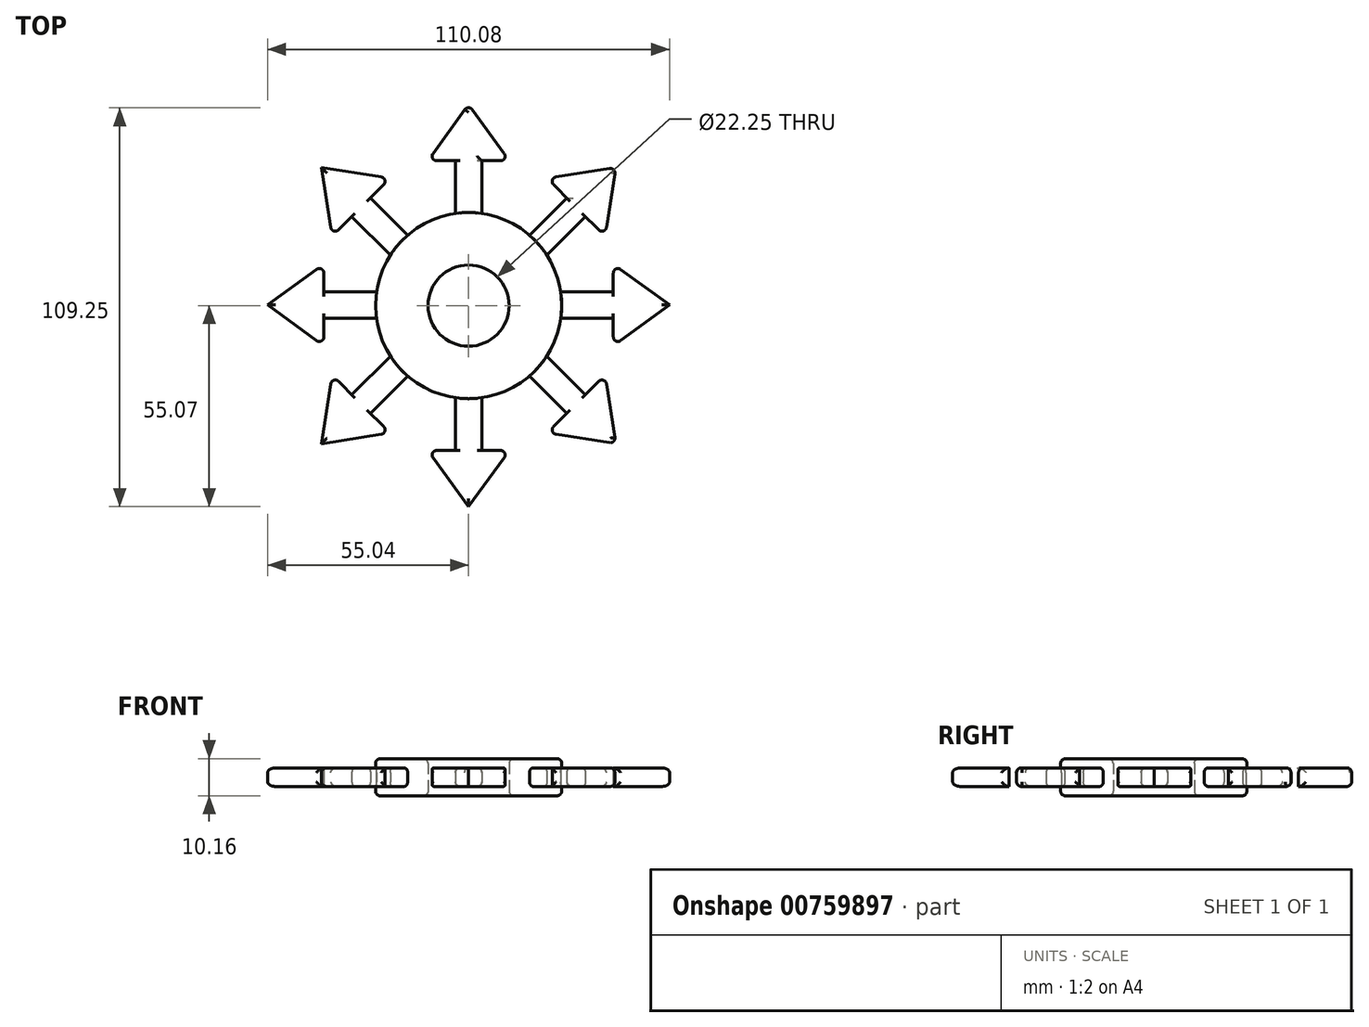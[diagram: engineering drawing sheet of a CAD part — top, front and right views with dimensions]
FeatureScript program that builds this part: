
annotation { "Feature Type Name" : "Feature", "Feature Type Description" : "" }
export const myFeature = defineFeature(function(context is Context, id is Id, definition is map)
    precondition{}
    {
        {
            var Q0;
            Q0=qCreatedBy(makeId("Top.planeOp"),FACE);
            var sketch = newSketch(context, id + "F0", { "sketchPlane" : qUnion([Q0])});
            skPoint(sketch, "E0.middle", {"position": v(0, 0) * mm});
            skCircle(sketch, "E1", {"center": v(0, 0) * mm, "radius": 25.5 * mm});
            skLineSegment(sketch, "E2", {"start": v(3.6, 25.24) * mm, "end": v(3.6, 39.67) * mm});
            skLineSegment(sketch, "E3", {"start": v(-3.6, 25.24) * mm, "end": v(-3.6, 39.67) * mm});
            skLineSegment(sketch, "E4", {"start": v(-3.6, 39.67) * mm, "end": v(-11.23, 39.67) * mm});
            skLineSegment(sketch, "E5", {"start": v(-11.23, 39.67) * mm, "end": v(0, 55.07) * mm});
            skLineSegment(sketch, "E6.MirrorCS", {"start": v(11.23, 39.67) * mm, "end": v(0, 55.07) * mm});
            skLineSegment(sketch, "E7.MirrorCS", {"start": v(3.6, 39.67) * mm, "end": v(11.23, 39.67) * mm});
            skLineSegment(sketch, "E8.MirrorCS", {"start": v(3.6, -25.24) * mm, "end": v(3.6, -39.67) * mm});
            skLineSegment(sketch, "E9.MirrorCS", {"start": v(-3.6, -25.24) * mm, "end": v(-3.6, -39.67) * mm});
            skLineSegment(sketch, "E10.MirrorCS", {"start": v(-11.23, -39.67) * mm, "end": v(0, -55.07) * mm});
            skLineSegment(sketch, "E11.MirrorCS", {"start": v(11.23, -39.67) * mm, "end": v(0, -55.07) * mm});
            skLineSegment(sketch, "E12.MirrorCS", {"start": v(3.6, -39.67) * mm, "end": v(11.23, -39.67) * mm});
            skLineSegment(sketch, "E13.MirrorCS", {"start": v(-3.6, -39.67) * mm, "end": v(-11.23, -39.67) * mm});
            skLineSegment(sketch, "E14", {"start": v(25.22, -3.44) * mm, "end": v(39.64, -3.44) * mm});
            skLineSegment(sketch, "E15", {"start": v(25.22, 3.77) * mm, "end": v(39.64, 3.77) * mm});
            skLineSegment(sketch, "E16", {"start": v(39.64, 3.77) * mm, "end": v(39.64, 11.4) * mm});
            skLineSegment(sketch, "E17", {"start": v(39.64, 11.4) * mm, "end": v(55.04, 0.17) * mm});
            skLineSegment(sketch, "E18.MirrorCS", {"start": v(39.64, -11.06) * mm, "end": v(55.04, 0.17) * mm});
            skLineSegment(sketch, "E19.MirrorCS", {"start": v(39.64, -3.44) * mm, "end": v(39.64, -11.06) * mm});
            skLineSegment(sketch, "E20.MirrorCS", {"start": v(-39.64, 11.4) * mm, "end": v(-55.04, 0.17) * mm});
            skLineSegment(sketch, "E21.MirrorCS", {"start": v(-39.64, -11.06) * mm, "end": v(-55.04, 0.17) * mm});
            skLineSegment(sketch, "E22.MirrorCS", {"start": v(-39.64, -3.44) * mm, "end": v(-39.64, -11.06) * mm});
            skLineSegment(sketch, "E23.MirrorCS", {"start": v(-39.64, 3.77) * mm, "end": v(-39.64, 11.4) * mm});
            skLineSegment(sketch, "E24.MirrorCS", {"start": v(-25.22, 3.77) * mm, "end": v(-39.64, 3.77) * mm});
            skLineSegment(sketch, "E25.MirrorCS", {"start": v(-25.22, -3.44) * mm, "end": v(-39.64, -3.44) * mm});
            skLineSegment(sketch, "E26", {"start": v(16.7, 19.28) * mm, "end": v(26.9, 29.48) * mm});
            skLineSegment(sketch, "E27", {"start": v(26.9, 29.48) * mm, "end": v(21.5, 34.86) * mm});
            skLineSegment(sketch, "E28", {"start": v(21.5, 34.86) * mm, "end": v(40.33, 37.82) * mm});
            skLineSegment(sketch, "E29.MirrorCS", {"start": v(37.38, 18.99) * mm, "end": v(40.33, 37.82) * mm});
            skLineSegment(sketch, "E30.MirrorCS", {"start": v(32, 24.38) * mm, "end": v(37.38, 18.99) * mm});
            skLineSegment(sketch, "E31.MirrorCS", {"start": v(-16.7, 19.28) * mm, "end": v(-26.9, 29.48) * mm});
            skLineSegment(sketch, "E32.MirrorCS", {"start": v(-37.38, 18.99) * mm, "end": v(-40.33, 37.82) * mm});
            skLineSegment(sketch, "E33.MirrorCS", {"start": v(-21.5, 34.86) * mm, "end": v(-40.33, 37.82) * mm});
            skLineSegment(sketch, "E34.MirrorCS", {"start": v(-26.9, 29.48) * mm, "end": v(-21.5, 34.86) * mm});
            skLineSegment(sketch, "E35.MirrorCS", {"start": v(-32, 24.38) * mm, "end": v(-37.38, 18.99) * mm});
            skLineSegment(sketch, "E36", {"start": v(-32, 24.38) * mm, "end": v(-21.43, 13.82) * mm});
            skLineSegment(sketch, "E37", {"start": v(32, 24.38) * mm, "end": v(21.43, 13.82) * mm});
            skLineSegment(sketch, "E38.MirrorCS", {"start": v(-16.7, -19.28) * mm, "end": v(-26.9, -29.48) * mm});
            skLineSegment(sketch, "E39.MirrorCS", {"start": v(-32, -24.38) * mm, "end": v(-21.43, -13.82) * mm});
            skLineSegment(sketch, "E40.MirrorCS", {"start": v(-37.38, -18.99) * mm, "end": v(-40.33, -37.82) * mm});
            skLineSegment(sketch, "E41.MirrorCS", {"start": v(-21.5, -34.86) * mm, "end": v(-40.33, -37.82) * mm});
            skLineSegment(sketch, "E42.MirrorCS", {"start": v(-26.9, -29.48) * mm, "end": v(-21.5, -34.86) * mm});
            skLineSegment(sketch, "E43.MirrorCS", {"start": v(-32, -24.38) * mm, "end": v(-37.38, -18.99) * mm});
            skLineSegment(sketch, "E44.MirrorCS", {"start": v(37.38, -18.99) * mm, "end": v(40.33, -37.82) * mm});
            skLineSegment(sketch, "E45.MirrorCS", {"start": v(21.5, -34.86) * mm, "end": v(40.33, -37.82) * mm});
            skLineSegment(sketch, "E46.MirrorCS", {"start": v(16.7, -19.28) * mm, "end": v(26.9, -29.48) * mm});
            skLineSegment(sketch, "E47.MirrorCS", {"start": v(32, -24.38) * mm, "end": v(21.43, -13.82) * mm});
            skLineSegment(sketch, "E48.MirrorCS", {"start": v(26.9, -29.48) * mm, "end": v(21.5, -34.86) * mm});
            skLineSegment(sketch, "E49.MirrorCS", {"start": v(32, -24.38) * mm, "end": v(37.38, -18.99) * mm});
            skCircle(sketch, "E50", {"center": v(0, 0) * mm, "radius": 11.13 * mm});
            skSolve(sketch);
        }
        {
            var Q0;
            Q0=makeQuery(id+"F0.imprint","IMPRINT",FACE,{"disambiguationData":[TD([[makeQuery(id+"F0.imprint","IMPRINT",EDGE,{"derivedFrom":sQuery(id+"F0.wireOp",EDGE,"E50")}),-1.0]])]});
            extrude(context, id + "F1", {"entities" : qUnion([Q0]), "endBound" : BoundingType.SYMMETRIC, "depth" : 10.16 * mm, "offsetDistance" : 25.4 * mm});
        }
        {
            var Q0;
            {var subQ0=sQuery(id+"F0.wireOp",EDGE,"E31.MirrorCS");Q0=makeQuery(id+"F0.imprint","IMPRINT",FACE,{"disambiguationData":[TD([[makeQuery(id+"F0.imprint","IMPRINT",EDGE,{"derivedFrom":subQ0}),1.0]])]});}
            var Q1;
            {var subQ1=sQuery(id+"F0.wireOp",EDGE,"E2");Q1=makeQuery(id+"F0.imprint","IMPRINT",FACE,{"disambiguationData":[TD([[makeQuery(id+"F0.imprint","IMPRINT",EDGE,{"derivedFrom":subQ1}),1.0]])]});}
            var Q2;
            {var subQ0=sQuery(id+"F0.wireOp",EDGE,"E26");Q2=makeQuery(id+"F0.imprint","IMPRINT",FACE,{"disambiguationData":[TD([[makeQuery(id+"F0.imprint","IMPRINT",EDGE,{"derivedFrom":subQ0}),-1.0]])]});}
            var Q3;
            {var subQ0=sQuery(id+"F0.wireOp",EDGE,"E15");Q3=makeQuery(id+"F0.imprint","IMPRINT",FACE,{"disambiguationData":[TD([[makeQuery(id+"F0.imprint","IMPRINT",EDGE,{"derivedFrom":subQ0}),-1.0]])]});}
            var Q4;
            Q4=makeQuery(id+"F0.imprint","IMPRINT",FACE,{"disambiguationData":[TD([[makeQuery(id+"F0.imprint","IMPRINT",EDGE,{"derivedFrom":sQuery(id+"F0.wireOp",EDGE,"E44.MirrorCS")}),-1.0]])]});
            var Q5;
            {var subQ1=sQuery(id+"F0.wireOp",EDGE,"E8.MirrorCS");Q5=makeQuery(id+"F0.imprint","IMPRINT",FACE,{"disambiguationData":[TD([[makeQuery(id+"F0.imprint","IMPRINT",EDGE,{"derivedFrom":subQ1}),-1.0]])]});}
            var Q6;
            {var subQ1=sQuery(id+"F0.wireOp",EDGE,"E38.MirrorCS");Q6=makeQuery(id+"F0.imprint","IMPRINT",FACE,{"disambiguationData":[TD([[makeQuery(id+"F0.imprint","IMPRINT",EDGE,{"derivedFrom":subQ1}),-1.0]])]});}
            var Q7;
            Q7=makeQuery(id+"F0.imprint","IMPRINT",FACE,{"disambiguationData":[TD([[makeQuery(id+"F0.imprint","IMPRINT",EDGE,{"derivedFrom":sQuery(id+"F0.wireOp",EDGE,"E20.MirrorCS")}),1.0]])]});
            extrude(context, id + "F2", {"entities" : qUnion([Q0, Q1, Q2, Q3, Q4, Q5, Q6, Q7]), "operationType" : NewBodyOperationType.ADD, "endBound" : BoundingType.SYMMETRIC, "depth" : 5.08 * mm, "offsetDistance" : 25.4 * mm});
        }
        {
            var Q0;
            Q0=makeQuery(id+"F1.opExtrude","CAP_FACE",FACE,{"disambiguationData":[OSD([sQuery(id+"F0.wireOp",EDGE,"E1"),sQuery(id+"F0.wireOp",EDGE,"E50")])],"isStart":false});
            var Q1;
            Q1=makeQuery(id+"F1.opExtrude","CAP_EDGE",EDGE,{"disambiguationData":[OSD([sQuery(id+"F0.wireOp",EDGE,"E1")])],"isStart":true});
            var Q2;
            Q2=makeQuery(id+"F2.opExtrude","CAP_EDGE",EDGE,{"disambiguationData":[OSD([sQuery(id+"F0.wireOp",EDGE,"E25.MirrorCS")])],"isStart":false});
            var Q3;
            Q3=makeQuery(id+"F2.opExtrude","CAP_EDGE",EDGE,{"disambiguationData":[OSD([sQuery(id+"F0.wireOp",EDGE,"E25.MirrorCS")])],"isStart":true});
            var Q4;
            Q4=makeQuery(id+"F2.opExtrude","CAP_EDGE",EDGE,{"disambiguationData":[OSD([sQuery(id+"F0.wireOp",EDGE,"E24.MirrorCS")])],"isStart":true});
            var Q5;
            Q5=makeQuery(id+"F2.opExtrude","CAP_EDGE",EDGE,{"disambiguationData":[OSD([sQuery(id+"F0.wireOp",EDGE,"E24.MirrorCS")])],"isStart":false});
            var Q6;
            Q6=makeQuery(id+"F2.opExtrude","CAP_EDGE",EDGE,{"disambiguationData":[OSD([sQuery(id+"F0.wireOp",EDGE,"E38.MirrorCS")])],"isStart":false});
            var Q7;
            Q7=makeQuery(id+"F2.opExtrude","CAP_EDGE",EDGE,{"disambiguationData":[OSD([sQuery(id+"F0.wireOp",EDGE,"E39.MirrorCS")])],"isStart":false});
            var Q8;
            Q8=makeQuery(id+"F2.opExtrude","CAP_EDGE",EDGE,{"disambiguationData":[OSD([sQuery(id+"F0.wireOp",EDGE,"E38.MirrorCS")])],"isStart":true});
            var Q9;
            Q9=makeQuery(id+"F2.opExtrude","CAP_EDGE",EDGE,{"disambiguationData":[OSD([sQuery(id+"F0.wireOp",EDGE,"E39.MirrorCS")])],"isStart":true});
            var Q10;
            Q10=makeQuery(id+"F2.opExtrude","CAP_EDGE",EDGE,{"disambiguationData":[OSD([sQuery(id+"F0.wireOp",EDGE,"E9.MirrorCS")])],"isStart":true});
            var Q11;
            Q11=makeQuery(id+"F2.opExtrude","CAP_EDGE",EDGE,{"disambiguationData":[OSD([sQuery(id+"F0.wireOp",EDGE,"E8.MirrorCS")])],"isStart":true});
            var Q12;
            Q12=makeQuery(id+"F2.opExtrude","CAP_EDGE",EDGE,{"disambiguationData":[OSD([sQuery(id+"F0.wireOp",EDGE,"E9.MirrorCS")])],"isStart":false});
            var Q13;
            Q13=makeQuery(id+"F2.opExtrude","CAP_EDGE",EDGE,{"disambiguationData":[OSD([sQuery(id+"F0.wireOp",EDGE,"E8.MirrorCS")])],"isStart":false});
            var Q14;
            Q14=makeQuery(id+"F2.opExtrude","CAP_EDGE",EDGE,{"disambiguationData":[OSD([sQuery(id+"F0.wireOp",EDGE,"E46.MirrorCS")])],"isStart":true});
            var Q15;
            Q15=makeQuery(id+"F2.opExtrude","CAP_EDGE",EDGE,{"disambiguationData":[OSD([sQuery(id+"F0.wireOp",EDGE,"E46.MirrorCS")])],"isStart":false});
            var Q16;
            Q16=makeQuery(id+"F2.opExtrude","CAP_EDGE",EDGE,{"disambiguationData":[OSD([sQuery(id+"F0.wireOp",EDGE,"E47.MirrorCS")])],"isStart":false});
            var Q17;
            Q17=makeQuery(id+"F2.opExtrude","CAP_EDGE",EDGE,{"disambiguationData":[OSD([sQuery(id+"F0.wireOp",EDGE,"E47.MirrorCS")])],"isStart":true});
            var Q18;
            Q18=makeQuery(id+"F2.opExtrude","CAP_EDGE",EDGE,{"disambiguationData":[OSD([sQuery(id+"F0.wireOp",EDGE,"E14")])],"isStart":true});
            var Q19;
            Q19=makeQuery(id+"F2.opExtrude","CAP_EDGE",EDGE,{"disambiguationData":[OSD([sQuery(id+"F0.wireOp",EDGE,"E14")])],"isStart":false});
            var Q20;
            Q20=makeQuery(id+"F2.opExtrude","CAP_EDGE",EDGE,{"disambiguationData":[OSD([sQuery(id+"F0.wireOp",EDGE,"E15")])],"isStart":true});
            var Q21;
            Q21=makeQuery(id+"F2.opExtrude","CAP_EDGE",EDGE,{"disambiguationData":[OSD([sQuery(id+"F0.wireOp",EDGE,"E15")])],"isStart":false});
            var Q22;
            Q22=makeQuery(id+"F2.opExtrude","CAP_EDGE",EDGE,{"disambiguationData":[OSD([sQuery(id+"F0.wireOp",EDGE,"E37")])],"isStart":true});
            var Q23;
            Q23=makeQuery(id+"F2.opExtrude","CAP_EDGE",EDGE,{"disambiguationData":[OSD([sQuery(id+"F0.wireOp",EDGE,"E37")])],"isStart":false});
            var Q24;
            Q24=makeQuery(id+"F2.opExtrude","CAP_EDGE",EDGE,{"disambiguationData":[OSD([sQuery(id+"F0.wireOp",EDGE,"E26")])],"isStart":true});
            var Q25;
            Q25=makeQuery(id+"F2.opExtrude","CAP_EDGE",EDGE,{"disambiguationData":[OSD([sQuery(id+"F0.wireOp",EDGE,"E26")])],"isStart":false});
            var Q26;
            Q26=makeQuery(id+"F2.opExtrude","CAP_EDGE",EDGE,{"disambiguationData":[OSD([sQuery(id+"F0.wireOp",EDGE,"E2")])],"isStart":true});
            var Q27;
            Q27=makeQuery(id+"F2.opExtrude","CAP_EDGE",EDGE,{"disambiguationData":[OSD([sQuery(id+"F0.wireOp",EDGE,"E2")])],"isStart":false});
            var Q28;
            Q28=makeQuery(id+"F2.opExtrude","CAP_EDGE",EDGE,{"disambiguationData":[OSD([sQuery(id+"F0.wireOp",EDGE,"E3")])],"isStart":false});
            var Q29;
            Q29=makeQuery(id+"F2.opExtrude","CAP_EDGE",EDGE,{"disambiguationData":[OSD([sQuery(id+"F0.wireOp",EDGE,"E3")])],"isStart":true});
            var Q30;
            Q30=makeQuery(id+"F2.opExtrude","CAP_EDGE",EDGE,{"disambiguationData":[OSD([sQuery(id+"F0.wireOp",EDGE,"E31.MirrorCS")])],"isStart":true});
            var Q31;
            Q31=makeQuery(id+"F2.opExtrude","CAP_EDGE",EDGE,{"disambiguationData":[OSD([sQuery(id+"F0.wireOp",EDGE,"E31.MirrorCS")])],"isStart":false});
            var Q32;
            Q32=makeQuery(id+"F2.opExtrude","CAP_EDGE",EDGE,{"disambiguationData":[OSD([sQuery(id+"F0.wireOp",EDGE,"E36")])],"isStart":true});
            var Q33;
            Q33=makeQuery(id+"F2.opExtrude","CAP_EDGE",EDGE,{"disambiguationData":[OSD([sQuery(id+"F0.wireOp",EDGE,"E36")])],"isStart":false});
            var Q34;
            Q34=makeQuery(id+"F2.opExtrude","CAP_EDGE",EDGE,{"disambiguationData":[OSD([sQuery(id+"F0.wireOp",EDGE,"E32.MirrorCS")])],"isStart":false});
            var Q35;
            Q35=makeQuery(id+"F2.opExtrude","CAP_EDGE",EDGE,{"disambiguationData":[OSD([sQuery(id+"F0.wireOp",EDGE,"E32.MirrorCS")])],"isStart":true});
            var Q36;
            Q36=makeQuery(id+"F2.opExtrude","CAP_EDGE",EDGE,{"disambiguationData":[OSD([sQuery(id+"F0.wireOp",EDGE,"E33.MirrorCS")])],"isStart":true});
            var Q37;
            Q37=makeQuery(id+"F2.opExtrude","CAP_EDGE",EDGE,{"disambiguationData":[OSD([sQuery(id+"F0.wireOp",EDGE,"E33.MirrorCS")])],"isStart":false});
            var Q38;
            Q38=makeQuery(id+"F2.opExtrude","SWEPT_EDGE",EDGE,{"disambiguationData":[OSD([sQuery(id+"F0.wireOp",EDGE,"E32.MirrorCS"),sQuery(id+"F0.wireOp",EDGE,"E35.MirrorCS")])]});
            var Q39;
            Q39=makeQuery(id+"F2.opExtrude","SWEPT_EDGE",EDGE,{"disambiguationData":[OSD([sQuery(id+"F0.wireOp",EDGE,"E33.MirrorCS"),sQuery(id+"F0.wireOp",EDGE,"E34.MirrorCS")])]});
            var Q40;
            Q40=makeQuery(id+"F2.opExtrude","SWEPT_EDGE",EDGE,{"disambiguationData":[OSD([sQuery(id+"F0.wireOp",EDGE,"E4"),sQuery(id+"F0.wireOp",EDGE,"E5")])]});
            var Q41;
            Q41=makeQuery(id+"F2.opExtrude","SWEPT_EDGE",EDGE,{"disambiguationData":[OSD([sQuery(id+"F0.wireOp",EDGE,"E6.MirrorCS"),sQuery(id+"F0.wireOp",EDGE,"E7.MirrorCS")])]});
            var Q42;
            Q42=makeQuery(id+"F2.opExtrude","CAP_EDGE",EDGE,{"disambiguationData":[OSD([sQuery(id+"F0.wireOp",EDGE,"E6.MirrorCS")])],"isStart":true});
            var Q43;
            Q43=makeQuery(id+"F2.opExtrude","CAP_EDGE",EDGE,{"disambiguationData":[OSD([sQuery(id+"F0.wireOp",EDGE,"E5")])],"isStart":false});
            var Q44;
            Q44=makeQuery(id+"F2.opExtrude","CAP_EDGE",EDGE,{"disambiguationData":[OSD([sQuery(id+"F0.wireOp",EDGE,"E5")])],"isStart":true});
            var Q45;
            Q45=makeQuery(id+"F2.opExtrude","CAP_EDGE",EDGE,{"disambiguationData":[OSD([sQuery(id+"F0.wireOp",EDGE,"E29.MirrorCS")])],"isStart":true});
            var Q46;
            Q46=makeQuery(id+"F2.opExtrude","CAP_EDGE",EDGE,{"disambiguationData":[OSD([sQuery(id+"F0.wireOp",EDGE,"E29.MirrorCS")])],"isStart":false});
            var Q47;
            Q47=makeQuery(id+"F2.opExtrude","CAP_EDGE",EDGE,{"disambiguationData":[OSD([sQuery(id+"F0.wireOp",EDGE,"E28")])],"isStart":false});
            var Q48;
            Q48=makeQuery(id+"F2.opExtrude","SWEPT_EDGE",EDGE,{"disambiguationData":[OSD([sQuery(id+"F0.wireOp",EDGE,"E27"),sQuery(id+"F0.wireOp",EDGE,"E28")])]});
            var Q49;
            Q49=makeQuery(id+"F2.opExtrude","SWEPT_EDGE",EDGE,{"disambiguationData":[OSD([sQuery(id+"F0.wireOp",EDGE,"E29.MirrorCS"),sQuery(id+"F0.wireOp",EDGE,"E30.MirrorCS")])]});
            var Q50;
            Q50=makeQuery(id+"F2.opExtrude","SWEPT_EDGE",EDGE,{"disambiguationData":[OSD([sQuery(id+"F0.wireOp",EDGE,"E16"),sQuery(id+"F0.wireOp",EDGE,"E17")])]});
            var Q51;
            Q51=makeQuery(id+"F2.opExtrude","SWEPT_EDGE",EDGE,{"disambiguationData":[OSD([sQuery(id+"F0.wireOp",EDGE,"E18.MirrorCS"),sQuery(id+"F0.wireOp",EDGE,"E19.MirrorCS")])]});
            var Q52;
            Q52=makeQuery(id+"F2.opExtrude","CAP_EDGE",EDGE,{"disambiguationData":[OSD([sQuery(id+"F0.wireOp",EDGE,"E18.MirrorCS")])],"isStart":false});
            var Q53;
            Q53=makeQuery(id+"F2.opExtrude","CAP_EDGE",EDGE,{"disambiguationData":[OSD([sQuery(id+"F0.wireOp",EDGE,"E17")])],"isStart":false});
            var Q54;
            Q54=makeQuery(id+"F2.opExtrude","CAP_EDGE",EDGE,{"disambiguationData":[OSD([sQuery(id+"F0.wireOp",EDGE,"E18.MirrorCS")])],"isStart":true});
            var Q55;
            Q55=makeQuery(id+"F2.opExtrude","CAP_EDGE",EDGE,{"disambiguationData":[OSD([sQuery(id+"F0.wireOp",EDGE,"E17")])],"isStart":true});
            var Q56;
            Q56=makeQuery(id+"F2.opExtrude","CAP_EDGE",EDGE,{"disambiguationData":[OSD([sQuery(id+"F0.wireOp",EDGE,"E44.MirrorCS")])],"isStart":false});
            var Q57;
            Q57=makeQuery(id+"F2.opExtrude","CAP_EDGE",EDGE,{"disambiguationData":[OSD([sQuery(id+"F0.wireOp",EDGE,"E44.MirrorCS")])],"isStart":true});
            var Q58;
            Q58=makeQuery(id+"F2.opExtrude","SWEPT_EDGE",EDGE,{"disambiguationData":[OSD([sQuery(id+"F0.wireOp",EDGE,"E44.MirrorCS"),sQuery(id+"F0.wireOp",EDGE,"E49.MirrorCS")])]});
            fillet(context, id + "F3", {"entities" : qUnion([Q0, Q1, Q2, Q3, Q4, Q5, Q6, Q7, Q8, Q9, Q10, Q11, Q12, Q13, Q14, Q15, Q16, Q17, Q18, Q19, Q20, Q21, Q22, Q23, Q24, Q25, Q26, Q27, Q28, Q29, Q30, Q31, Q32, Q33, Q34, Q35, Q36, Q37, Q38, Q39, Q40, Q41, Q42, Q43, Q44, Q45, Q46, Q47, Q48, Q49, Q50, Q51, Q52, Q53, Q54, Q55, Q56, Q57, Q58]), "radius" : 1.27 * mm, "tangentPropagation" : true, "allowEdgeOverflow" : false});
        }
        {
            var Q0;
            Q0=makeQuery(id+"F2.opExtrude","CAP_EDGE",EDGE,{"disambiguationData":[OSD([sQuery(id+"F0.wireOp",EDGE,"E45.MirrorCS")])],"isStart":true});
            var Q1;
            Q1=makeQuery(id+"F2.opExtrude","CAP_EDGE",EDGE,{"disambiguationData":[OSD([sQuery(id+"F0.wireOp",EDGE,"E45.MirrorCS")])],"isStart":false});
            var Q2;
            Q2=makeQuery(id+"F2.opExtrude","SWEPT_EDGE",EDGE,{"disambiguationData":[OSD([sQuery(id+"F0.wireOp",EDGE,"E45.MirrorCS"),sQuery(id+"F0.wireOp",EDGE,"E48.MirrorCS")])]});
            var Q3;
            Q3=makeQuery(id+"F2.opExtrude","SWEPT_EDGE",EDGE,{"disambiguationData":[OSD([sQuery(id+"F0.wireOp",EDGE,"E11.MirrorCS"),sQuery(id+"F0.wireOp",EDGE,"E12.MirrorCS")])]});
            var Q4;
            Q4=makeQuery(id+"F2.opExtrude","CAP_EDGE",EDGE,{"disambiguationData":[OSD([sQuery(id+"F0.wireOp",EDGE,"E11.MirrorCS")])],"isStart":false});
            var Q5;
            Q5=makeQuery(id+"F2.opExtrude","CAP_EDGE",EDGE,{"disambiguationData":[OSD([sQuery(id+"F0.wireOp",EDGE,"E11.MirrorCS")])],"isStart":true});
            var Q6;
            Q6=makeQuery(id+"F2.opExtrude","SWEPT_EDGE",EDGE,{"disambiguationData":[OSD([sQuery(id+"F0.wireOp",EDGE,"E10.MirrorCS"),sQuery(id+"F0.wireOp",EDGE,"E13.MirrorCS")])]});
            var Q7;
            Q7=makeQuery(id+"F2.opExtrude","CAP_EDGE",EDGE,{"disambiguationData":[OSD([sQuery(id+"F0.wireOp",EDGE,"E10.MirrorCS")])],"isStart":true});
            var Q8;
            Q8=makeQuery(id+"F2.opExtrude","CAP_EDGE",EDGE,{"disambiguationData":[OSD([sQuery(id+"F0.wireOp",EDGE,"E10.MirrorCS")])],"isStart":false});
            var Q9;
            Q9=makeQuery(id+"F2.opExtrude","SWEPT_EDGE",EDGE,{"disambiguationData":[OSD([sQuery(id+"F0.wireOp",EDGE,"E41.MirrorCS"),sQuery(id+"F0.wireOp",EDGE,"E42.MirrorCS")])]});
            var Q10;
            Q10=makeQuery(id+"F2.opExtrude","CAP_EDGE",EDGE,{"disambiguationData":[OSD([sQuery(id+"F0.wireOp",EDGE,"E41.MirrorCS")])],"isStart":true});
            var Q11;
            Q11=makeQuery(id+"F2.opExtrude","CAP_EDGE",EDGE,{"disambiguationData":[OSD([sQuery(id+"F0.wireOp",EDGE,"E41.MirrorCS")])],"isStart":false});
            var Q12;
            Q12=makeQuery(id+"F2.opExtrude","SWEPT_EDGE",EDGE,{"disambiguationData":[OSD([sQuery(id+"F0.wireOp",EDGE,"E40.MirrorCS"),sQuery(id+"F0.wireOp",EDGE,"E43.MirrorCS")])]});
            var Q13;
            Q13=makeQuery(id+"F2.opExtrude","CAP_EDGE",EDGE,{"disambiguationData":[OSD([sQuery(id+"F0.wireOp",EDGE,"E40.MirrorCS")])],"isStart":true});
            var Q14;
            Q14=makeQuery(id+"F2.opExtrude","CAP_EDGE",EDGE,{"disambiguationData":[OSD([sQuery(id+"F0.wireOp",EDGE,"E40.MirrorCS")])],"isStart":false});
            var Q15;
            Q15=makeQuery(id+"F2.opExtrude","SWEPT_EDGE",EDGE,{"disambiguationData":[OSD([sQuery(id+"F0.wireOp",EDGE,"E20.MirrorCS"),sQuery(id+"F0.wireOp",EDGE,"E23.MirrorCS")])]});
            var Q16;
            Q16=makeQuery(id+"F2.opExtrude","CAP_EDGE",EDGE,{"disambiguationData":[OSD([sQuery(id+"F0.wireOp",EDGE,"E20.MirrorCS")])],"isStart":true});
            var Q17;
            Q17=makeQuery(id+"F2.opExtrude","CAP_EDGE",EDGE,{"disambiguationData":[OSD([sQuery(id+"F0.wireOp",EDGE,"E21.MirrorCS")])],"isStart":false});
            var Q18;
            Q18=makeQuery(id+"F2.opExtrude","CAP_EDGE",EDGE,{"disambiguationData":[OSD([sQuery(id+"F0.wireOp",EDGE,"E21.MirrorCS")])],"isStart":true});
            var Q19;
            Q19=makeQuery(id+"F2.opExtrude","SWEPT_EDGE",EDGE,{"disambiguationData":[OSD([sQuery(id+"F0.wireOp",EDGE,"E21.MirrorCS"),sQuery(id+"F0.wireOp",EDGE,"E22.MirrorCS")])]});
            var Q20;
            Q20=makeQuery(id+"F2.opExtrude","CAP_EDGE",EDGE,{"disambiguationData":[OSD([sQuery(id+"F0.wireOp",EDGE,"E20.MirrorCS")])],"isStart":false});
            var Q21;
            Q21=makeQuery(id+"F2.opExtrude","CAP_EDGE",EDGE,{"disambiguationData":[OSD([sQuery(id+"F0.wireOp",EDGE,"E28")])],"isStart":true});
            var Q22;
            Q22=makeQuery(id+"F2.opExtrude","CAP_EDGE",EDGE,{"disambiguationData":[OSD([sQuery(id+"F0.wireOp",EDGE,"E6.MirrorCS")])],"isStart":false});
            var Q23;
            Q23=makeQuery(id+"F1.opExtrude","CAP_EDGE",EDGE,{"disambiguationData":[OSD([sQuery(id+"F0.wireOp",EDGE,"E50")])],"isStart":true});
            var Q24;
            {var subQ0=sQuery(id+"F0.wireOp",EDGE,"E50");Q24=makeQuery(id+"F3.opFillet","BLEND_EDGE",EDGE,{"blendedFrom":[makeQuery(id+"F1.opExtrude","CAP_EDGE",EDGE,{"disambiguationData":[OSD([subQ0])],"isStart":false}),makeQuery(id+"F1.opExtrude","SWEPT_FACE",FACE,{"disambiguationData":[OSD([subQ0])]})],"blendedInto":[makeQuery(id+"F1.opExtrude","SWEPT_FACE",FACE,{"disambiguationData":[OSD([subQ0])]})]});}
            fillet(context, id + "F4", {"entities" : qUnion([Q0, Q1, Q2, Q3, Q4, Q5, Q6, Q7, Q8, Q9, Q10, Q11, Q12, Q13, Q14, Q15, Q16, Q17, Q18, Q19, Q20, Q21, Q22, Q23, Q24]), "radius" : 1.27 * mm, "tangentPropagation" : true, "allowEdgeOverflow" : false});
        }
    });
